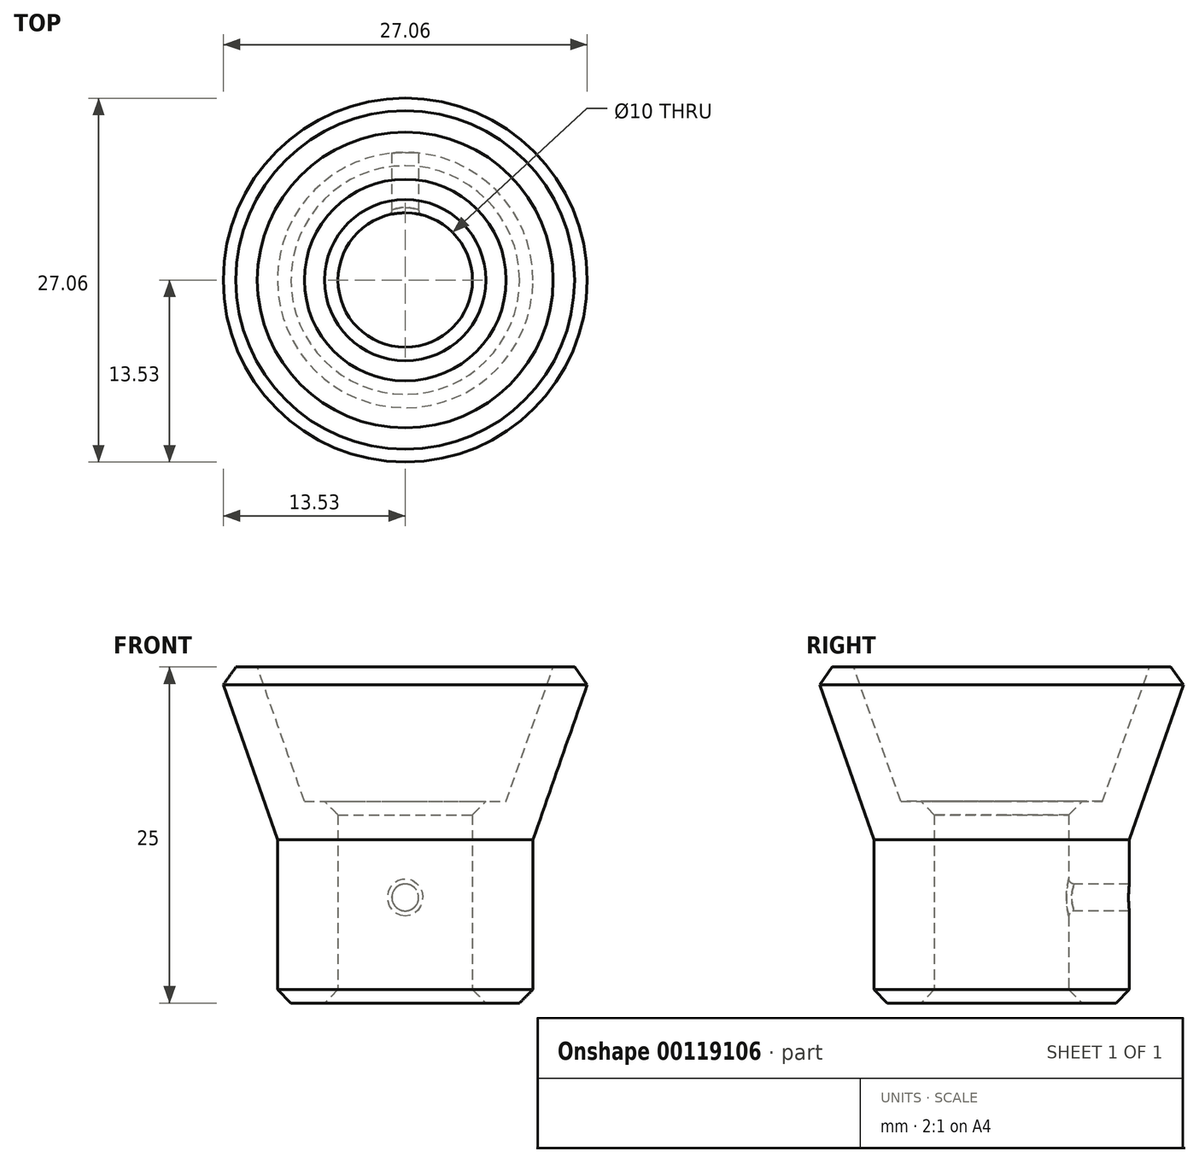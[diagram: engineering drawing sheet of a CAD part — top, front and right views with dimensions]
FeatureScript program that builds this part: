
annotation { "Feature Type Name" : "Feature", "Feature Type Description" : "" }
export const myFeature = defineFeature(function(context is Context, id is Id, definition is map)
    precondition{}
    {
        {
            var Q0;
            Q0=qCreatedBy(makeId("Front.planeOp"),FACE);
            var sketch = newSketch(context, id + "F0", { "sketchPlane" : qUnion([Q0])});
            skLineSegment(sketch, "E0", {"start": v(0, 0) * mm, "end": v(0, 30) * mm, "construction": true});
            skLineSegment(sketch, "E1", {"start": v(0, 0) * mm, "end": v(5, 0) * mm, "construction": true});
            skLineSegment(sketch, "E2", {"start": v(5, 0) * mm, "end": v(5, 15) * mm});
            skLineSegment(sketch, "E3", {"start": v(5, 15) * mm, "end": v(7.5, 15) * mm});
            skLineSegment(sketch, "E4", {"start": v(0, 25) * mm, "end": v(11, 25) * mm, "construction": true});
            skLineSegment(sketch, "E5", {"start": v(11, 25) * mm, "end": v(7.5, 15) * mm});
            skLineSegment(sketch, "E6", {"start": v(11, 25) * mm, "end": v(14, 25) * mm});
            skLineSegment(sketch, "E7", {"start": v(14, 25) * mm, "end": v(10.5, 15) * mm});
            skLineSegment(sketch, "E8", {"start": v(10.5, 15) * mm, "end": v(10.5, 0) * mm});
            skLineSegment(sketch, "E9", {"start": v(10.5, 0) * mm, "end": v(5, 0) * mm});
            skSolve(sketch);
        }
        {
            var Q0;
            Q0=makeQuery(id+"F0.imprint","IMPRINT",FACE,{"disambiguationData":[TD([[makeQuery(id+"F0.imprint","IMPRINT",EDGE,{"derivedFrom":sQuery(id+"F0.wireOp",EDGE,"E2")}),-1.0]])]});
            var Q1;
            Q1=sQuery(id+"F0.wireOp",EDGE,"E0");
            revolve(context, id + "F1", {"entities" : qUnion([Q0]), "axis" : qUnion([Q1]), "revolveType" : RevolveType.FULL});
        }
        {
            var Q0;
            Q0=makeQuery(id+"F1.opRevolve","SWEPT_EDGE",EDGE,{"disambiguationData":[OSD([sQuery(id+"F0.wireOp",EDGE,"E6"),sQuery(id+"F0.wireOp",EDGE,"E7")])]});
            var Q1;
            Q1=makeQuery(id+"F1.opRevolve","SWEPT_EDGE",EDGE,{"disambiguationData":[OSD([sQuery(id+"F0.wireOp",EDGE,"E2"),sQuery(id+"F0.wireOp",EDGE,"E3")])]});
            var Q2;
            Q2=makeQuery(id+"F1.opRevolve","SWEPT_EDGE",EDGE,{"disambiguationData":[OSD([sQuery(id+"F0.wireOp",EDGE,"E2"),sQuery(id+"F0.wireOp",EDGE,"E9")])]});
            var Q3;
            Q3=makeQuery(id+"F1.opRevolve","SWEPT_EDGE",EDGE,{"disambiguationData":[OSD([sQuery(id+"F0.wireOp",EDGE,"E8"),sQuery(id+"F0.wireOp",EDGE,"E9")])]});
            chamfer(context, id + "F2", {"entities" : qUnion([Q0, Q1, Q2, Q3]), "width" : 1 * mm, "tangentPropagation" : true});
        }
        {
            var Q0;
            Q0=qCreatedBy(makeId("Front.planeOp"),FACE);
            var sketch = newSketch(context, id + "F3", { "sketchPlane" : qUnion([Q0])});
            skLineSegment(sketch, "E10", {"start": v(10.5, 15) * mm, "end": v(10.5, 0.7) * mm});
            skLineSegment(sketch, "E11", {"start": v(-10.5, 0.7) * mm, "end": v(-10.5, 15) * mm});
            skPoint(sketch, "E12", {"position": v(0, 7.85) * mm});
            skPoint(sketch, "E12.positionSnap0", {"position": v(-10.5, 7.85) * mm});
            skCircle(sketch, "E13", {"center": v(0, 7.85) * mm, "radius": 1 * mm});
            skSolve(sketch);
        }
        {
            var Q0;
            Q0=makeQuery(id+"F3.imprint","IMPRINT",FACE,{"disambiguationData":[TD([[makeQuery(id+"F3.imprint","IMPRINT",EDGE,{"derivedFrom":sQuery(id+"F3.wireOp",EDGE,"E13")}),1.0]])]});
            extrude(context, id + "F4", {"entities" : qUnion([Q0]), "operationType" : NewBodyOperationType.REMOVE, "endBound" : BoundingType.THROUGH_ALL, "oppositeDirection" : true, "depth" : 25 * mm});
        }
        {
            var Q0;
            Q0=makeQuery(id+"F4.boolean.opBoolean","INTERSECT",EDGE,{"derivedFrom":[makeQuery(id+"F1.opRevolve","SWEPT_FACE",FACE,{"disambiguationData":[OSD([sQuery(id+"F0.wireOp",EDGE,"E8")])]}),makeQuery(id+"F4.opExtrude","SWEPT_FACE",FACE,{"disambiguationData":[OSD([sQuery(id+"F3.wireOp",EDGE,"E13")])]})]});
            var Q1;
            Q1=makeQuery(id+"F4.boolean.opBoolean","INTERSECT",EDGE,{"derivedFrom":[makeQuery(id+"F1.opRevolve","SWEPT_FACE",FACE,{"disambiguationData":[OSD([sQuery(id+"F0.wireOp",EDGE,"E2")])]}),makeQuery(id+"F4.opExtrude","SWEPT_FACE",FACE,{"disambiguationData":[OSD([sQuery(id+"F3.wireOp",EDGE,"E13")])]})]});
            fillet(context, id + "F5", {"entities" : qUnion([Q0, Q1]), "radius" : .4 * mm, "tangentPropagation" : true, "allowEdgeOverflow" : false});
        }
        {
            var Q0;
            Q0=makeQuery(id+"F1.opRevolve","SWEPT_FACE",FACE,{"disambiguationData":[OSD([sQuery(id+"F0.wireOp",EDGE,"E9")])]});
            var sketch = newSketch(context, id + "F6", { "sketchPlane" : qUnion([Q0])});
            skCircle(sketch, "E14.0", {"center": v(0, 0) * mm, "radius": 10.5 * mm});
            skCircle(sketch, "E15", {"center": v(0, 0) * mm, "radius": 9.5 * mm});
            skSolve(sketch);
        }
        {
            var Q0;
            Q0=makeQuery(id+"F6.imprint","IMPRINT",FACE,{"disambiguationData":[TD([[makeQuery(id+"F6.imprint","IMPRINT",EDGE,{"derivedFrom":sQuery(id+"F6.wireOp",EDGE,"E14.0")}),1.0]])]});
            var Q1;
            Q1=makeQuery(id+"F1.opRevolve","SWEPT_FACE",FACE,{"disambiguationData":[OSD([sQuery(id+"F0.wireOp",EDGE,"E7")])]});
            extrude(context, id + "F7", {"entities" : qUnion([Q0]), "operationType" : NewBodyOperationType.REMOVE, "endBound" : BoundingType.UP_TO_SURFACE, "oppositeDirection" : true, "endBoundEntityFace" : qUnion([Q1]), "depth" : 25 * mm});
        }
        {
            var Q0;
            {var subQ0=sQuery(id+"F0.wireOp",EDGE,"E9");var subQ1=sQuery(id+"F0.wireOp",EDGE,"E8");Q0=makeQuery(id+"F7.boolean.opBoolean","MERGE",EDGE,{"derivedFrom":[makeQuery(id+"F2.opChamfer","BLEND_EDGE",EDGE,{"blendedFrom":[makeQuery(id+"F1.opRevolve","SWEPT_EDGE",EDGE,{"disambiguationData":[OSD([subQ1,subQ0])]}),makeQuery(id+"F1.opRevolve","SWEPT_FACE",FACE,{"disambiguationData":[OSD([subQ0])]})],"blendedInto":[makeQuery(id+"F1.opRevolve","SWEPT_FACE",FACE,{"disambiguationData":[OSD([subQ0])]})]}),makeQuery(id+"F7.opExtrude","CAP_EDGE",EDGE,{"disambiguationData":[OSD([subQ1,subQ0])],"isStart":true})]});}
            chamfer(context, id + "F8", {"entities" : qUnion([Q0]), "width" : 1 * mm, "tangentPropagation" : true});
        }
    });
